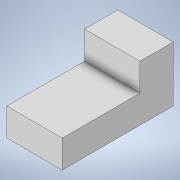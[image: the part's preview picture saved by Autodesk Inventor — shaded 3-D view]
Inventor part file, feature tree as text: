
AUTODESK INVENTOR PART (.ipt)
format: ipt  version: 2021 (Build 250183000, 183)  size: 92,160 bytes
history: native  units: mm
features: other x1, extrude x1, sketch x1
ambient origin geometry x8: Origin, YZ Plane, XZ Plane, XY Plane, X Axis, Y Axis, Z Axis, Center Point
bodies: Body1 (feature_tree)
feature tree (3):
  other  "Sólido1"
  extrude  "Extrusão1"  Depth=30.0mm
  sketch  "Esboço3"  dims[d0=60.0mm d1=30.0mm d2=18.0mm d3=15.0mm d4=30.0mm d5=0.0mm]
